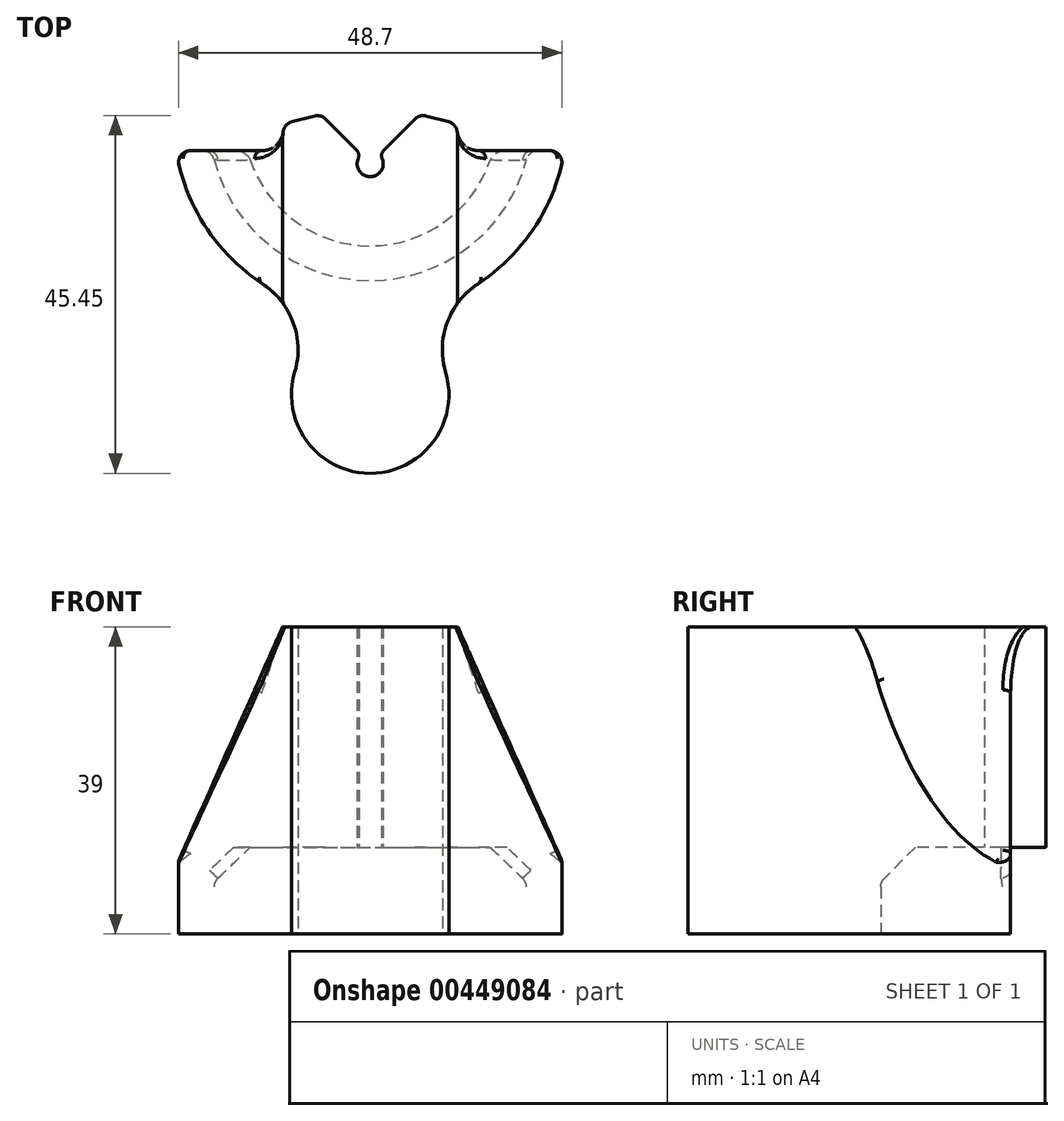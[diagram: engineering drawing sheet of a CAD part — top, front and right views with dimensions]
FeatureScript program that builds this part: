
annotation { "Feature Type Name" : "Feature", "Feature Type Description" : "" }
export const myFeature = defineFeature(function(context is Context, id is Id, definition is map)
    precondition{}
    {
        {
            var Q0;
            Q0=qCreatedBy(makeId("Top.planeOp"),FACE);
            var sketch = newSketch(context, id + "F0", { "sketchPlane" : qUnion([Q0])});
            skCircle(sketch, "E0", {"center": v(0, 0) * mm, "radius": 10 * mm, "construction": true});
            skArc(sketch, "E1", {"start": v(-20.1, -4) * mm, "mid": v(0, -20.5) * mm, "end": v(20.1, -4) * mm});
            skCircle(sketch, "E2", {"center": v(0, 0) * mm, "radius": 4 * mm, "construction": true});
            skLineSegment(sketch, "E3", {"start": v(-24.68, -4) * mm, "end": v(-20.1, -4) * mm});
            skArc(sketch, "E4", {"start": v(-24.68, -4) * mm, "mid": v(-20.97, -13.62) * mm, "end": v(-13.7, -20.92) * mm});
            skLineSegment(sketch, "E5.trimOffspring", {"start": v(20.1, -4) * mm, "end": v(24.68, -4) * mm});
            skArc(sketch, "E6", {"start": v(-9.58, -32.14) * mm, "mid": v(0, -45) * mm, "end": v(9.58, -32.14) * mm});
            skArc(sketch, "E7", {"start": v(-9.58, -32.14) * mm, "mid": v(-9.78, -25.85) * mm, "end": v(-13.7, -20.92) * mm});
            skArc(sketch, "E8", {"start": v(13.7, -20.92) * mm, "mid": v(9.78, -25.85) * mm, "end": v(9.58, -32.14) * mm});
            skArc(sketch, "E9.trimOffspring", {"start": v(13.7, -20.92) * mm, "mid": v(20.97, -13.62) * mm, "end": v(24.68, -4) * mm});
            skSolve(sketch);
        }
        {
            var Q0;
            Q0 = qSketchRegion(id + "F0", true);
            extrude(context, id + "F1", {"entities" : qUnion([Q0]), "depth" : 6.6 * mm});
        }
        {
            var Q0;
            Q0=makeQuery(id+"F1.opExtrude","CAP_FACE",FACE,{"disambiguationData":[OSD([sQuery(id+"F0.wireOp",EDGE,"E1"),sQuery(id+"F0.wireOp",EDGE,"E3"),sQuery(id+"F0.wireOp",EDGE,"E4"),sQuery(id+"F0.wireOp",EDGE,"E5.trimOffspring"),sQuery(id+"F0.wireOp",EDGE,"E6"),sQuery(id+"F0.wireOp",EDGE,"E7"),sQuery(id+"F0.wireOp",EDGE,"E8"),sQuery(id+"F0.wireOp",EDGE,"E9.trimOffspring")])],"isStart":false});
            var sketch = newSketch(context, id + "F2", { "sketchPlane" : qUnion([Q0])});
            skArc(sketch, "E10.0.0", {"start": v(9.58, -32.14) * mm, "mid": v(9.78, -25.85) * mm, "end": v(13.7, -20.92) * mm});
            skArc(sketch, "E10.0.1", {"start": v(13.7, -20.92) * mm, "mid": v(20.97, -13.62) * mm, "end": v(24.68, -4) * mm});
            skLineSegment(sketch, "E10.0.2", {"start": v(24.68, -4) * mm, "end": v(20.1, -4) * mm});
            skLineSegment(sketch, "E10.0.4", {"start": v(-20.1, -4) * mm, "end": v(-24.68, -4) * mm});
            skArc(sketch, "E10.0.5", {"start": v(-24.68, -4) * mm, "mid": v(-20.97, -13.62) * mm, "end": v(-13.7, -20.92) * mm});
            skArc(sketch, "E10.0.6", {"start": v(-13.7, -20.92) * mm, "mid": v(-9.78, -25.85) * mm, "end": v(-9.58, -32.14) * mm});
            skArc(sketch, "E10.0.7", {"start": v(-9.58, -32.14) * mm, "mid": v(0, -45) * mm, "end": v(9.58, -32.14) * mm});
            skArc(sketch, "E11.0", {"start": v(15.6, -4) * mm, "mid": v(0, -16.1) * mm, "end": v(-15.6, -4) * mm});
            skLineSegment(sketch, "E12", {"start": v(-20.1, -4) * mm, "end": v(-15.6, -4) * mm});
            skLineSegment(sketch, "E13.trimOffspring", {"start": v(15.6, -4) * mm, "end": v(20.1, -4) * mm});
            skSolve(sketch);
        }
        {
            var Q0;
            Q0 = qSketchRegion(id + "F2", true);
            extrude(context, id + "F3", {"entities" : qUnion([Q0]), "operationType" : NewBodyOperationType.ADD, "depth" : 4.4 * mm});
        }
        {
            var Q0;
            Q0=makeQuery(id+"F3.opExtrude","CAP_FACE",FACE,{"disambiguationData":[OSD([sQuery(id+"F2.wireOp",EDGE,"E10.0.0"),sQuery(id+"F2.wireOp",EDGE,"E10.0.1"),sQuery(id+"F2.wireOp",EDGE,"E10.0.2"),sQuery(id+"F2.wireOp",EDGE,"E10.0.4"),sQuery(id+"F2.wireOp",EDGE,"E10.0.5"),sQuery(id+"F2.wireOp",EDGE,"E10.0.6"),sQuery(id+"F2.wireOp",EDGE,"E10.0.7"),sQuery(id+"F2.wireOp",EDGE,"E11.0"),sQuery(id+"F2.wireOp",EDGE,"E12"),sQuery(id+"F2.wireOp",EDGE,"E13.trimOffspring")])],"isStart":false});
            var sketch = newSketch(context, id + "F4", { "sketchPlane" : qUnion([Q0])});
            skLineSegment(sketch, "E14", {"start": v(-6.27, 0.6) * mm, "end": v(-1.17, -4.49) * mm});
            skLineSegment(sketch, "E15", {"start": v(1.17, -4.49) * mm, "end": v(6.27, 0.6) * mm});
            skLineSegment(sketch, "E16", {"start": v(6.27, 0.6) * mm, "end": v(24.68, -4) * mm, "construction": true});
            skLineSegment(sketch, "E17", {"start": v(-24.68, -4) * mm, "end": v(-6.27, 0.6) * mm, "construction": true});
            skArc(sketch, "E18", {"start": v(-1.17, -4.49) * mm, "mid": v(0, -7.31) * mm, "end": v(1.17, -4.49) * mm});
            skArc(sketch, "E19.0", {"start": v(-24.68, -4) * mm, "mid": v(-20.97, -13.62) * mm, "end": v(-13.7, -20.92) * mm});
            skArc(sketch, "E20.0", {"start": v(-9.58, -32.14) * mm, "mid": v(-9.78, -25.85) * mm, "end": v(-13.7, -20.92) * mm});
            skArc(sketch, "E21.0", {"start": v(-9.58, -32.14) * mm, "mid": v(0, -45) * mm, "end": v(9.58, -32.14) * mm});
            skArc(sketch, "E22.0", {"start": v(13.7, -20.92) * mm, "mid": v(9.78, -25.85) * mm, "end": v(9.58, -32.14) * mm});
            skArc(sketch, "E23.0", {"start": v(13.7, -20.92) * mm, "mid": v(20.97, -13.62) * mm, "end": v(24.68, -4) * mm});
            skLineSegment(sketch, "E24", {"start": v(-24.68, -4) * mm, "end": v(-13.77, -4) * mm});
            skLineSegment(sketch, "E25", {"start": v(24.68, -4) * mm, "end": v(13.77, -4) * mm});
            skArc(sketch, "E26", {"start": v(11.12, -0.6) * mm, "mid": v(11.61, -2.95) * mm, "end": v(13.77, -4) * mm});
            skArc(sketch, "E27", {"start": v(-13.77, -4) * mm, "mid": v(-11.61, -2.95) * mm, "end": v(-11.12, -0.6) * mm});
            skLineSegment(sketch, "E28", {"start": v(-6.27, 0.6) * mm, "end": v(-11.12, -0.6) * mm});
            skLineSegment(sketch, "E29", {"start": v(6.27, 0.6) * mm, "end": v(11.12, -0.6) * mm});
            skSolve(sketch);
        }
        {
            var Q0;
            Q0 = qSketchRegion(id + "F4", true);
            extrude(context, id + "F5", {"entities" : qUnion([Q0]), "operationType" : NewBodyOperationType.ADD, "depth" : 28 * mm});
        }
        {
            var Q0;
            Q0=makeQuery(id+"F5.boolean.opBoolean","MERGE",FACE,{"derivedFrom":[makeQuery(id+"F3.boolean.opBoolean","MERGE",FACE,{"derivedFrom":[makeQuery(id+"F1.opExtrude","SWEPT_FACE",FACE,{"disambiguationData":[OSD([sQuery(id+"F0.wireOp",EDGE,"E5.trimOffspring")])]}),makeQuery(id+"F3.opExtrude","SWEPT_FACE",FACE,{"disambiguationData":[OSD([sQuery(id+"F2.wireOp",EDGE,"E10.0.2"),sQuery(id+"F2.wireOp",EDGE,"E13.trimOffspring")])]})]}),makeQuery(id+"F5.opExtrude","SWEPT_FACE",FACE,{"disambiguationData":[OSD([sQuery(id+"F4.wireOp",EDGE,"E25")])]})]});
            var sketch = newSketch(context, id + "F6", { "sketchPlane" : qUnion([Q0])});
            skLineSegment(sketch, "E30", {"start": v(-24.68, 8.54) * mm, "end": v(-11.12, 39) * mm});
            skLineSegment(sketch, "E31", {"start": v(-11.12, 39) * mm, "end": v(-24.68, 39) * mm});
            skLineSegment(sketch, "E32", {"start": v(-24.68, 39) * mm, "end": v(-24.68, 8.54) * mm});
            skLineSegment(sketch, "E33", {"start": v(0, 0) * mm, "end": v(0, 39) * mm, "construction": true});
            skLineSegment(sketch, "E34.MirrorCS", {"start": v(24.68, 39) * mm, "end": v(24.68, 8.54) * mm});
            skLineSegment(sketch, "E35.MirrorCS", {"start": v(24.68, 8.54) * mm, "end": v(11.12, 39) * mm});
            skLineSegment(sketch, "E36.MirrorCS", {"start": v(11.12, 39) * mm, "end": v(24.68, 39) * mm});
            skSolve(sketch);
        }
        {
            var Q0;
            Q0 = qSketchRegion(id + "F6", true);
            extrude(context, id + "F7", {"entities" : qUnion([Q0]), "operationType" : NewBodyOperationType.REMOVE, "endBound" : BoundingType.SYMMETRIC, "depth" : 100 * mm});
        }
        {
            var Q0;
            Q0=makeQuery(id+"F3.opExtrude","CAP_EDGE",EDGE,{"disambiguationData":[OSD([sQuery(id+"F2.wireOp",EDGE,"E11.0")])],"isStart":true});
            chamfer(context, id + "F8", {"entities" : qUnion([Q0]), "width" : 4.4 * mm, "tangentPropagation" : true});
        }
        {
            var Q0;
            Q0=makeQuery(id+"F5.boolean.opBoolean","MERGE",EDGE,{"derivedFrom":[makeQuery(id+"F3.boolean.opBoolean","MERGE",EDGE,{"derivedFrom":[makeQuery(id+"F1.opExtrude","SWEPT_EDGE",EDGE,{"disambiguationData":[OSD([sQuery(id+"F0.wireOp",EDGE,"E5.trimOffspring"),sQuery(id+"F0.wireOp",EDGE,"E9.trimOffspring")])]}),makeQuery(id+"F3.opExtrude","SWEPT_EDGE",EDGE,{"disambiguationData":[OSD([sQuery(id+"F2.wireOp",EDGE,"E10.0.1"),sQuery(id+"F2.wireOp",EDGE,"E10.0.2")])]})]}),makeQuery(id+"F5.opExtrude","SWEPT_EDGE",EDGE,{"disambiguationData":[OSD([sQuery(id+"F4.wireOp",EDGE,"E23.0"),sQuery(id+"F4.wireOp",EDGE,"E25")])]})]});
            var Q1;
            Q1=makeQuery(id+"F5.boolean.opBoolean","MERGE",EDGE,{"derivedFrom":[makeQuery(id+"F3.boolean.opBoolean","MERGE",EDGE,{"derivedFrom":[makeQuery(id+"F1.opExtrude","SWEPT_EDGE",EDGE,{"disambiguationData":[OSD([sQuery(id+"F0.wireOp",EDGE,"E3"),sQuery(id+"F0.wireOp",EDGE,"E4")])]}),makeQuery(id+"F3.opExtrude","SWEPT_EDGE",EDGE,{"disambiguationData":[OSD([sQuery(id+"F2.wireOp",EDGE,"E10.0.4"),sQuery(id+"F2.wireOp",EDGE,"E10.0.5")])]})]}),makeQuery(id+"F5.opExtrude","SWEPT_EDGE",EDGE,{"disambiguationData":[OSD([sQuery(id+"F4.wireOp",EDGE,"E19.0"),sQuery(id+"F4.wireOp",EDGE,"E24")])]})]});
            var Q2;
            Q2=makeQuery(id+"F5.opExtrude","SWEPT_EDGE",EDGE,{"disambiguationData":[OSD([sQuery(id+"F4.wireOp",EDGE,"E27"),sQuery(id+"F4.wireOp",EDGE,"E28")])]});
            var Q3;
            Q3=makeQuery(id+"F5.opExtrude","SWEPT_EDGE",EDGE,{"disambiguationData":[OSD([sQuery(id+"F4.wireOp",EDGE,"E26"),sQuery(id+"F4.wireOp",EDGE,"E29")])]});
            var Q4;
            Q4=makeQuery(id+"F5.opExtrude","SWEPT_EDGE",EDGE,{"disambiguationData":[OSD([sQuery(id+"F4.wireOp",EDGE,"E15"),sQuery(id+"F4.wireOp",EDGE,"E29")])]});
            var Q5;
            Q5=makeQuery(id+"F5.opExtrude","SWEPT_EDGE",EDGE,{"disambiguationData":[OSD([sQuery(id+"F4.wireOp",EDGE,"E14"),sQuery(id+"F4.wireOp",EDGE,"E28")])]});
            var Q6;
            Q6=makeQuery(id+"F1.opExtrude","SWEPT_EDGE",EDGE,{"disambiguationData":[OSD([sQuery(id+"F0.wireOp",EDGE,"E1"),sQuery(id+"F0.wireOp",EDGE,"E3")])]});
            var Q7;
            Q7=makeQuery(id+"F8.opChamfer","BLEND_EDGE",EDGE,{"blendedFrom":[makeQuery(id+"F3.opExtrude","CAP_EDGE",EDGE,{"disambiguationData":[OSD([sQuery(id+"F2.wireOp",EDGE,"E11.0")])],"isStart":true}),makeQuery(id+"F5.boolean.opBoolean","MERGE",FACE,{"derivedFrom":[makeQuery(id+"F3.boolean.opBoolean","MERGE",FACE,{"derivedFrom":[makeQuery(id+"F1.opExtrude","SWEPT_FACE",FACE,{"disambiguationData":[OSD([sQuery(id+"F0.wireOp",EDGE,"E3")])]}),makeQuery(id+"F3.opExtrude","SWEPT_FACE",FACE,{"disambiguationData":[OSD([sQuery(id+"F2.wireOp",EDGE,"E10.0.4"),sQuery(id+"F2.wireOp",EDGE,"E12")])]})]}),makeQuery(id+"F5.opExtrude","SWEPT_FACE",FACE,{"disambiguationData":[OSD([sQuery(id+"F4.wireOp",EDGE,"E24")])]})]})],"blendedInto":[makeQuery(id+"F5.boolean.opBoolean","MERGE",FACE,{"derivedFrom":[makeQuery(id+"F3.boolean.opBoolean","MERGE",FACE,{"derivedFrom":[makeQuery(id+"F1.opExtrude","SWEPT_FACE",FACE,{"disambiguationData":[OSD([sQuery(id+"F0.wireOp",EDGE,"E3")])]}),makeQuery(id+"F3.opExtrude","SWEPT_FACE",FACE,{"disambiguationData":[OSD([sQuery(id+"F2.wireOp",EDGE,"E10.0.4"),sQuery(id+"F2.wireOp",EDGE,"E12")])]})]}),makeQuery(id+"F5.opExtrude","SWEPT_FACE",FACE,{"disambiguationData":[OSD([sQuery(id+"F4.wireOp",EDGE,"E24")])]})]})]});
            var Q8;
            Q8=makeQuery(id+"F1.opExtrude","SWEPT_EDGE",EDGE,{"disambiguationData":[OSD([sQuery(id+"F0.wireOp",EDGE,"E1"),sQuery(id+"F0.wireOp",EDGE,"E5.trimOffspring")])]});
            var Q9;
            Q9=makeQuery(id+"F8.opChamfer","BLEND_EDGE",EDGE,{"blendedFrom":[makeQuery(id+"F3.opExtrude","CAP_EDGE",EDGE,{"disambiguationData":[OSD([sQuery(id+"F2.wireOp",EDGE,"E11.0")])],"isStart":true}),makeQuery(id+"F5.boolean.opBoolean","MERGE",FACE,{"derivedFrom":[makeQuery(id+"F3.boolean.opBoolean","MERGE",FACE,{"derivedFrom":[makeQuery(id+"F1.opExtrude","SWEPT_FACE",FACE,{"disambiguationData":[OSD([sQuery(id+"F0.wireOp",EDGE,"E5.trimOffspring")])]}),makeQuery(id+"F3.opExtrude","SWEPT_FACE",FACE,{"disambiguationData":[OSD([sQuery(id+"F2.wireOp",EDGE,"E10.0.2"),sQuery(id+"F2.wireOp",EDGE,"E13.trimOffspring")])]})]}),makeQuery(id+"F5.opExtrude","SWEPT_FACE",FACE,{"disambiguationData":[OSD([sQuery(id+"F4.wireOp",EDGE,"E25")])]})]})],"blendedInto":[makeQuery(id+"F5.boolean.opBoolean","MERGE",FACE,{"derivedFrom":[makeQuery(id+"F3.boolean.opBoolean","MERGE",FACE,{"derivedFrom":[makeQuery(id+"F1.opExtrude","SWEPT_FACE",FACE,{"disambiguationData":[OSD([sQuery(id+"F0.wireOp",EDGE,"E5.trimOffspring")])]}),makeQuery(id+"F3.opExtrude","SWEPT_FACE",FACE,{"disambiguationData":[OSD([sQuery(id+"F2.wireOp",EDGE,"E10.0.2"),sQuery(id+"F2.wireOp",EDGE,"E13.trimOffspring")])]})]}),makeQuery(id+"F5.opExtrude","SWEPT_FACE",FACE,{"disambiguationData":[OSD([sQuery(id+"F4.wireOp",EDGE,"E25")])]})]})]});
            var Q10;
            Q10=makeQuery(id+"F8.opChamfer","BLEND_EDGE",EDGE,{"blendedFrom":[makeQuery(id+"F3.opExtrude","CAP_EDGE",EDGE,{"disambiguationData":[OSD([sQuery(id+"F2.wireOp",EDGE,"E11.0")])],"isStart":true}),makeQuery(id+"F1.opExtrude","SWEPT_FACE",FACE,{"disambiguationData":[OSD([sQuery(id+"F0.wireOp",EDGE,"E1")])]})],"blendedInto":[makeQuery(id+"F1.opExtrude","SWEPT_FACE",FACE,{"disambiguationData":[OSD([sQuery(id+"F0.wireOp",EDGE,"E1")])]})]});
            fillet(context, id + "F9", {"entities" : qUnion([Q0, Q1, Q2, Q3, Q4, Q5, Q6, Q7, Q8, Q9, Q10]), "radius" : 1.5 * mm, "tangentPropagation" : true, "allowEdgeOverflow" : false});
        }
        {
            var Q0;
            Q0=makeQuery(id+"F5.opExtrude","SWEPT_EDGE",EDGE,{"disambiguationData":[OSD([sQuery(id+"F4.wireOp",EDGE,"E14"),sQuery(id+"F4.wireOp",EDGE,"E18")])]});
            var Q1;
            Q1=makeQuery(id+"F5.opExtrude","SWEPT_EDGE",EDGE,{"disambiguationData":[OSD([sQuery(id+"F4.wireOp",EDGE,"E15"),sQuery(id+"F4.wireOp",EDGE,"E18")])]});
            var Q2;
            Q2=makeQuery(id+"F7.boolean.opBoolean","INTERSECT",EDGE,{"derivedFrom":[makeQuery(id+"F5.boolean.opBoolean","MERGE",FACE,{"derivedFrom":[makeQuery(id+"F3.boolean.opBoolean","MERGE",FACE,{"derivedFrom":[makeQuery(id+"F1.opExtrude","SWEPT_FACE",FACE,{"disambiguationData":[OSD([sQuery(id+"F0.wireOp",EDGE,"E9.trimOffspring")])]}),makeQuery(id+"F3.opExtrude","SWEPT_FACE",FACE,{"disambiguationData":[OSD([sQuery(id+"F2.wireOp",EDGE,"E10.0.1")])]})]}),makeQuery(id+"F5.opExtrude","SWEPT_FACE",FACE,{"disambiguationData":[OSD([sQuery(id+"F4.wireOp",EDGE,"E23.0")])]})]}),makeQuery(id+"F7.opExtrude","SWEPT_FACE",FACE,{"disambiguationData":[OSD([sQuery(id+"F6.wireOp",EDGE,"E30")])]})]});
            var Q3;
            Q3=makeQuery(id+"F7.boolean.opBoolean","INTERSECT",EDGE,{"derivedFrom":[makeQuery(id+"F5.boolean.opBoolean","MERGE",FACE,{"derivedFrom":[makeQuery(id+"F3.boolean.opBoolean","MERGE",FACE,{"derivedFrom":[makeQuery(id+"F1.opExtrude","SWEPT_FACE",FACE,{"disambiguationData":[OSD([sQuery(id+"F0.wireOp",EDGE,"E3")])]}),makeQuery(id+"F3.opExtrude","SWEPT_FACE",FACE,{"disambiguationData":[OSD([sQuery(id+"F2.wireOp",EDGE,"E10.0.4"),sQuery(id+"F2.wireOp",EDGE,"E12")])]})]}),makeQuery(id+"F5.opExtrude","SWEPT_FACE",FACE,{"disambiguationData":[OSD([sQuery(id+"F4.wireOp",EDGE,"E24")])]})]}),makeQuery(id+"F7.opExtrude","SWEPT_FACE",FACE,{"disambiguationData":[OSD([sQuery(id+"F6.wireOp",EDGE,"E35.MirrorCS")])]})]});
            fillet(context, id + "F10", {"entities" : qUnion([Q0, Q1, Q2, Q3]), "radius" : 1 * mm, "tangentPropagation" : true, "allowEdgeOverflow" : false});
        }
    });
